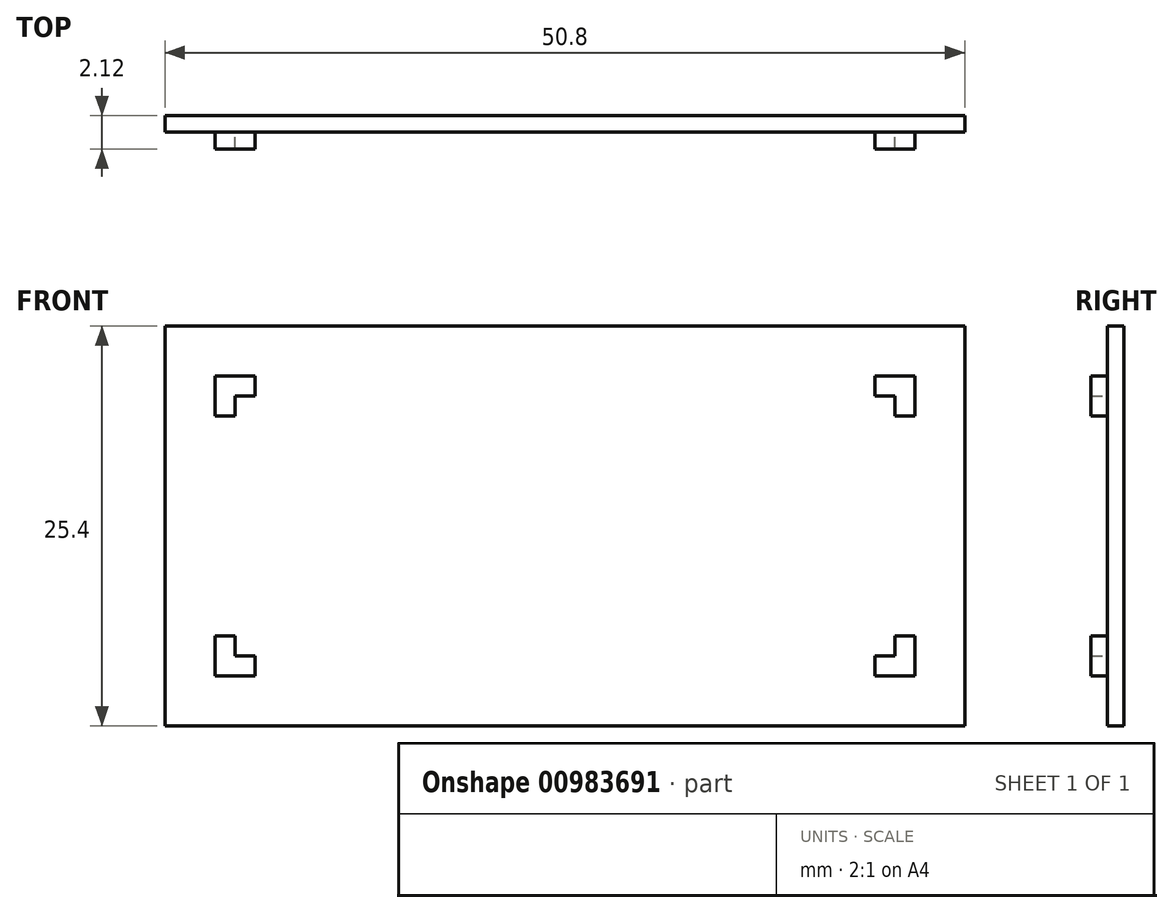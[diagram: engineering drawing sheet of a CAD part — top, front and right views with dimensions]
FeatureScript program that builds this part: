
annotation { "Feature Type Name" : "Feature", "Feature Type Description" : "" }
export const myFeature = defineFeature(function(context is Context, id is Id, definition is map)
    precondition{}
    {
        {
            var Q0;
            Q0=qCreatedBy(makeId("Front.planeOp"),FACE);
            var sketch = newSketch(context, id + "F0", { "sketchPlane" : qUnion([Q0])});
            skLineSegment(sketch, "E0.bottom", {"start": v(25.4, 12.7) * mm, "end": v(-25.4, 12.7) * mm});
            skLineSegment(sketch, "E0.top", {"start": v(25.4, -12.7) * mm, "end": v(-25.4, -12.7) * mm});
            skLineSegment(sketch, "E0.left", {"start": v(25.4, 12.7) * mm, "end": v(25.4, -12.7) * mm});
            skLineSegment(sketch, "E0.right", {"start": v(-25.4, 12.7) * mm, "end": v(-25.4, -12.7) * mm});
            skPoint(sketch, "E0.middle", {"position": v(0, 0) * mm});
            skSolve(sketch);
        }
        {
            var Q0;
            Q0 = qSketchRegion(id + "F0", true);
            extrude(context, id + "F1", {"entities" : qUnion([Q0]), "depth" : 1.06 * mm, "offsetDistance" : 25.4 * mm});
        }
        {
            var Q0;
            Q0=qCreatedBy(makeId("Front.planeOp"),FACE);
            var sketch = newSketch(context, id + "F2", { "sketchPlane" : qUnion([Q0])});
            skLineSegment(sketch, "E1.bottom", {"start": v(22.22, 9.53) * mm, "end": v(19.68, 9.53) * mm});
            skLineSegment(sketch, "E1.top", {"start": v(22.23, -9.53) * mm, "end": v(19.69, -9.53) * mm});
            skLineSegment(sketch, "E1.left", {"start": v(22.22, 9.53) * mm, "end": v(22.23, 6.99) * mm});
            skLineSegment(sketch, "E1.right", {"start": v(-22.23, 9.53) * mm, "end": v(-22.23, 6.98) * mm});
            skPoint(sketch, "E1.middle", {"position": v(0, 0) * mm});
            skLineSegment(sketch, "E2.bottom", {"start": v(20.95, 8.26) * mm, "end": v(19.68, 8.26) * mm});
            skLineSegment(sketch, "E2.top", {"start": v(20.95, -8.26) * mm, "end": v(19.69, -8.26) * mm});
            skLineSegment(sketch, "E2.left", {"start": v(20.95, 8.26) * mm, "end": v(20.95, 6.99) * mm});
            skLineSegment(sketch, "E2.right", {"start": v(-20.96, 8.26) * mm, "end": v(-20.96, 6.98) * mm});
            skLineSegment(sketch, "E3", {"start": v(-22.23, 6.98) * mm, "end": v(-20.96, 6.98) * mm});
            skLineSegment(sketch, "E4", {"start": v(-19.69, -8.26) * mm, "end": v(-19.69, -9.53) * mm});
            skLineSegment(sketch, "E5", {"start": v(-20.96, -6.99) * mm, "end": v(-22.23, -6.99) * mm});
            skLineSegment(sketch, "E6", {"start": v(19.68, 9.53) * mm, "end": v(19.68, 8.26) * mm});
            skLineSegment(sketch, "E7", {"start": v(20.95, 6.99) * mm, "end": v(22.22, 6.99) * mm});
            skLineSegment(sketch, "E8", {"start": v(19.69, -8.26) * mm, "end": v(19.69, -9.52) * mm});
            skLineSegment(sketch, "E9", {"start": v(20.95, -6.98) * mm, "end": v(22.23, -6.98) * mm});
            skLineSegment(sketch, "E10", {"start": v(-19.69, 8.26) * mm, "end": v(-19.69, 9.52) * mm});
            skLineSegment(sketch, "E11.trimOffspring", {"start": v(-19.69, 8.26) * mm, "end": v(-20.96, 8.26) * mm});
            skLineSegment(sketch, "E12.trimOffspring", {"start": v(-19.69, 9.53) * mm, "end": v(-22.23, 9.53) * mm});
            skLineSegment(sketch, "E13.trimOffspring", {"start": v(-20.96, -6.99) * mm, "end": v(-20.96, -8.26) * mm});
            skLineSegment(sketch, "E14.trimOffspring", {"start": v(-22.23, -6.99) * mm, "end": v(-22.23, -9.53) * mm});
            skLineSegment(sketch, "E15.trimOffspring", {"start": v(-19.68, -8.26) * mm, "end": v(-20.96, -8.26) * mm});
            skLineSegment(sketch, "E16.trimOffspring", {"start": v(-19.69, -9.53) * mm, "end": v(-22.23, -9.53) * mm});
            skLineSegment(sketch, "E17.trimOffspring", {"start": v(20.95, -6.98) * mm, "end": v(20.95, -8.26) * mm});
            skLineSegment(sketch, "E18.trimOffspring", {"start": v(22.23, -6.98) * mm, "end": v(22.23, -9.53) * mm});
            skSolve(sketch);
        }
        {
            var Q0;
            Q0 = qSketchRegion(id + "F2", true);
            extrude(context, id + "F3", {"entities" : qUnion([Q0]), "operationType" : NewBodyOperationType.ADD, "depth" : 2.12 * mm, "offsetDistance" : 25.4 * mm});
        }
    });
